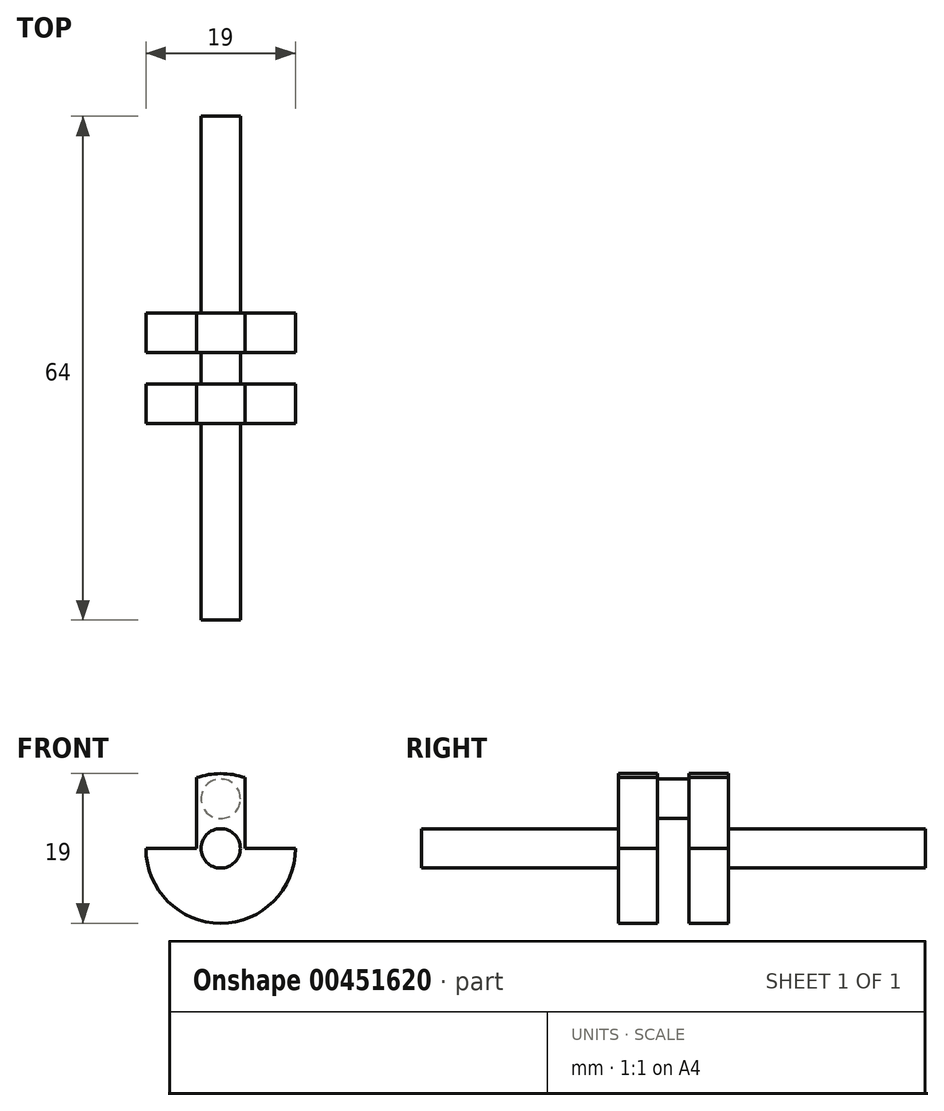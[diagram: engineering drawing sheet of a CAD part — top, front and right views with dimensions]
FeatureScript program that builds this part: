
annotation { "Feature Type Name" : "Feature", "Feature Type Description" : "" }
export const myFeature = defineFeature(function(context is Context, id is Id, definition is map)
    precondition{}
    {
        {
            var Q0;
            Q0=qCreatedBy(makeId("Front.planeOp"),FACE);
            var sketch = newSketch(context, id + "F0", { "sketchPlane" : qUnion([Q0])});
            skPoint(sketch, "E0", {"position": v(0, 6.3) * mm});
            skLineSegment(sketch, "E1.left", {"start": v(3.08, -8.99) * mm, "end": v(3.08, 8.99) * mm});
            skLineSegment(sketch, "E1.right", {"start": v(-3.08, -8.99) * mm, "end": v(-3.08, 8.99) * mm});
            skPoint(sketch, "E1.middle", {"position": v(0, 0) * mm});
            skArc(sketch, "E2", {"start": v(-3.08, 8.99) * mm, "mid": v(0, 9.5) * mm, "end": v(3.08, 8.99) * mm});
            skPoint(sketch, "E3", {"position": v(0, 9.5) * mm});
            skArc(sketch, "E4", {"start": v(3.08, 8.99) * mm, "mid": v(0, 9.5) * mm, "end": v(-3.08, 8.99) * mm});
            skLineSegment(sketch, "E5", {"start": v(3.08, 0) * mm, "end": v(9.5, 0) * mm});
            skLineSegment(sketch, "E6", {"start": v(-3.08, 0) * mm, "end": v(-9.5, 0) * mm});
            skArc(sketch, "E7.trimOffspring", {"start": v(-9.5, 0) * mm, "mid": v(0, -9.5) * mm, "end": v(9.5, 0) * mm});
            skSolve(sketch);
        }
        {
            var Q0;
            Q0=makeQuery(id+"F0.imprint","IMPRINT",FACE,{"disambiguationData":[TD([[makeQuery(id+"F0.imprint","IMPRINT",EDGE,{"derivedFrom":sQuery(id+"F0.wireOp",EDGE,"E1.left")}),1.0]])]});
            var Q1;
            Q1=qSketchRegion(id+"F2",true);
            var Q2;
            {var subQ3=sQuery(id+"F0.wireOp",EDGE,"E6");Q2=makeQuery(id+"F0.imprint","IMPRINT",FACE,{"disambiguationData":[TD([[makeQuery(id+"F0.imprint","IMPRINT",EDGE,{"derivedFrom":subQ3}),1.0]])]});}
            var Q3;
            {var subQ3=sQuery(id+"F0.wireOp",EDGE,"E5");Q3=makeQuery(id+"F0.imprint","IMPRINT",FACE,{"disambiguationData":[TD([[makeQuery(id+"F0.imprint","IMPRINT",EDGE,{"derivedFrom":subQ3}),-1.0]])]});}
            extrude(context, id + "F1", {"entities" : qUnion([Q0, Q1, Q2, Q3]), "endBound" : BoundingType.SYMMETRIC, "depth" : 5 * mm});
        }
        {
            var Q0;
            Q0=makeQuery(id+"F1.opExtrude","CAP_FACE",FACE,{"disambiguationData":[OSD([sQuery(id+"F0.wireOp",EDGE,"E1.left"),sQuery(id+"F0.wireOp",EDGE,"E1.right"),sQuery(id+"F0.wireOp",EDGE,"E2"),sQuery(id+"F0.wireOp",EDGE,"VFhB1kta-8bxy-pE8t-JsMO-NGhGx0J8nSL1")])],"isStart":false});
            var sketch = newSketch(context, id + "F2", { "sketchPlane" : qUnion([Q0])});
            skPoint(sketch, "E8", {"position": v(0, 0) * mm});
            skPoint(sketch, "E9", {"position": v(0, 6.3) * mm});
            skCircle(sketch, "E10", {"center": v(0, 6.3) * mm, "radius": 2.5 * mm});
            skCircle(sketch, "E11", {"center": v(0, 0) * mm, "radius": 2.5 * mm});
            skSolve(sketch);
        }
        {
            var Q0;
            Q0=makeQuery(id+"F1.opExtrude","SWEPT_BODY",BODY,{"disambiguationData":[OSD([sQuery(id+"F0.wireOp",EDGE,"E1.left"),sQuery(id+"F0.wireOp",EDGE,"E1.right"),sQuery(id+"F0.wireOp",EDGE,"E2"),sQuery(id+"F0.wireOp",EDGE,"VFhB1kta-8bxy-pE8t-JsMO-NGhGx0J8nSL1")])]});
            transform(context, id + "F3", {"entities" : qUnion([Q0]), "transformType" : TransformType.TRANSLATION_3D, "dx" : 0 * mm, "dy" : 9 * mm, "dz" : 0 * mm, "makeCopy" : true});
        }
        {
            var Q0;
            Q0=makeQuery(id+"F2.imprint","IMPRINT",FACE,{"disambiguationData":[TD([[makeQuery(id+"F2.imprint","IMPRINT",EDGE,{"derivedFrom":sQuery(id+"F2.wireOp",EDGE,"E10")}),1.0]])]});
            var Q1;
            Q1=sQuery(id+"F2.wireOp",EDGE,"E10");
            var Q2;
            Q2=makeQuery(id+"F3.opPattern","COPY",FACE,{"derivedFrom":makeQuery(id+"F1.opExtrude","CAP_FACE",FACE,{"disambiguationData":[OSD([sQuery(id+"F0.wireOp",EDGE,"E1.left"),sQuery(id+"F0.wireOp",EDGE,"E1.right"),sQuery(id+"F0.wireOp",EDGE,"E2"),sQuery(id+"F0.wireOp",EDGE,"VFhB1kta-8bxy-pE8t-JsMO-NGhGx0J8nSL1")])],"isStart":true}),"instanceName":"1"});
            extrude(context, id + "F4", {"entities" : qUnion([Q0]), "operationType" : NewBodyOperationType.ADD, "surfaceEntities" : qUnion([Q1]), "endBound" : BoundingType.UP_TO_SURFACE, "oppositeDirection" : true, "endBoundEntityFace" : qUnion([Q2]), "depth" : 25 * mm});
        }
        {
            var Q0;
            Q0=makeQuery(id+"F1.opExtrude","CAP_FACE",FACE,{"disambiguationData":[OSD([sQuery(id+"F0.wireOp",EDGE,"E1.left"),sQuery(id+"F0.wireOp",EDGE,"E1.right"),sQuery(id+"F0.wireOp",EDGE,"E2"),sQuery(id+"F0.wireOp",EDGE,"VFhB1kta-8bxy-pE8t-JsMO-NGhGx0J8nSL1")])],"isStart":true});
            var sketch = newSketch(context, id + "F5", { "sketchPlane" : qUnion([Q0])});
            skCircle(sketch, "E12", {"center": v(0, 0) * mm, "radius": 2.5 * mm});
            skSolve(sketch);
        }
        {
            var Q0;
            Q0=makeQuery(id+"F5.imprint","IMPRINT",FACE,{"disambiguationData":[TD([[makeQuery(id+"F5.imprint","IMPRINT",EDGE,{"derivedFrom":sQuery(id+"F5.wireOp",EDGE,"E12")}),1.0]])]});
            extrude(context, id + "F6", {"entities" : qUnion([Q0]), "operationType" : NewBodyOperationType.ADD, "oppositeDirection" : true, "depth" : 30 * mm});
        }
        {
            var Q0;
            Q0=makeQuery(id+"F3.opPattern","COPY",FACE,{"derivedFrom":makeQuery(id+"F1.opExtrude","CAP_FACE",FACE,{"disambiguationData":[OSD([sQuery(id+"F0.wireOp",EDGE,"E1.left"),sQuery(id+"F0.wireOp",EDGE,"E1.right"),sQuery(id+"F0.wireOp",EDGE,"E2"),sQuery(id+"F0.wireOp",EDGE,"VFhB1kta-8bxy-pE8t-JsMO-NGhGx0J8nSL1")])],"isStart":false}),"instanceName":"1"});
            var sketch = newSketch(context, id + "F7", { "sketchPlane" : qUnion([Q0])});
            skCircle(sketch, "E13", {"center": v(0, 0) * mm, "radius": 2.5 * mm});
            skSolve(sketch);
        }
        {
            var Q0;
            Q0=makeQuery(id+"F7.imprint","IMPRINT",FACE,{"disambiguationData":[TD([[makeQuery(id+"F7.imprint","IMPRINT",EDGE,{"derivedFrom":sQuery(id+"F7.wireOp",EDGE,"E13")}),1.0]])]});
            extrude(context, id + "F8", {"entities" : qUnion([Q0]), "operationType" : NewBodyOperationType.ADD, "oppositeDirection" : true, "depth" : 30 * mm});
        }
    });
